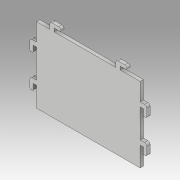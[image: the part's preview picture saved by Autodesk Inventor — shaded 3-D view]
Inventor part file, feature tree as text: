
AUTODESK INVENTOR PART (.ipt)
format: ipt  version: 2019.3 (Build 233278000, 278)  size: 167,936 bytes
history: native  units: mm
features: extrude x1, sketch x1
ambient origin geometry x8: Origin, YZ Plane, XZ Plane, XY Plane, X Axis, Y Axis, Z Axis, Center Point
bodies: Solid1 (feature_tree)
feature tree (2):
  extrude  "Extrusion1"  Depth=68.0mm
  sketch  "Sketch1"  dims[d0=94.0mm d1=68.0mm d2=7.0mm d3=12.0mm d4=12.0mm d7=53.0mm d8=10.0mm d9=3.0mm d10=3.0mm d11=6.0mm d12=18.0mm d13=48.0mm d14=2.0mm d15=1.0mm d16=10.0mm d17=3.0mm d18=3.0mm d19=6.0mm d20=18.0mm d21=78.0mm d22=2.0mm d23=1.0mm d24=3.0mm d25=0.0mm]
